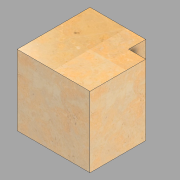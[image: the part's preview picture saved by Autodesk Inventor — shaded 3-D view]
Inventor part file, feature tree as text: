
AUTODESK INVENTOR PART (.ipt)
format: ipt  version: 2022.2 (Build 262287000, 287)  size: 140,288 bytes
history: native  units: in
note: dims shown in document units (in); Inventor stores cm internally (conversion verified against a paired STEP export)
features: extrude x2, sketch x2
ambient origin geometry x8: Origin, YZ Plane, XZ Plane, XY Plane, X Axis, Y Axis, Z Axis, Center Point
bodies: Solid1 (feature_tree)
feature tree (4):
  extrude  "Extrusion1"  Depth=8.0in
  extrude  "Extrusion2"  Depth=1.875in
  sketch  "Sketch1"  dims[d0=8.0in d1=8.0in]
  sketch  "Sketch2"  dims[d2=7.75in d3=0.0in d4=1.875in d5=1.875in d6=0.0in d7=0.0in]
